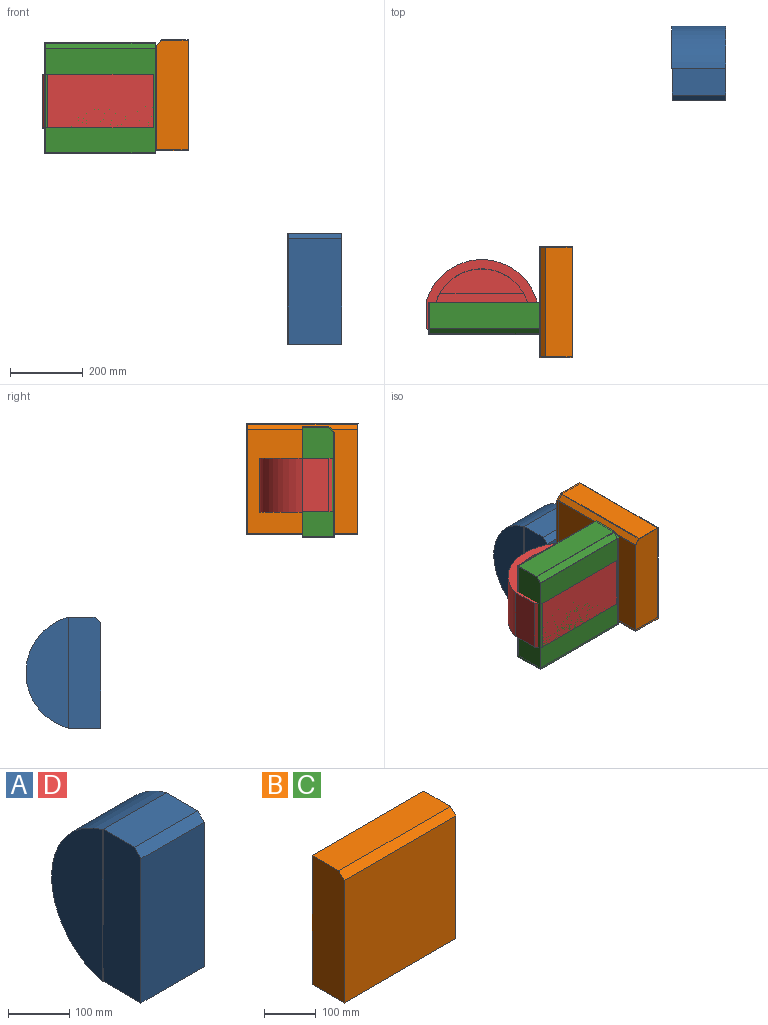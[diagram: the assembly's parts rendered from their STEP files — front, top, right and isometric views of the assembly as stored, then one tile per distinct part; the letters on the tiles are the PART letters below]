
ASSEMBLY  parts=4 mates=2
PART A: 17 faces, bbox 148.6x205x304.8 mm
  f0: plane 304.8x2.03mm, normal (0,-1,0), area 619.4mm2, adj f1,f3,f8
  f1: cylinder r=157.75mm len=304.8mm, axis (-1,0,0), area 61394.1mm2, adj f0,f2,f3,f5,f6
  f2: plane 304.8x205.01mm, normal (1,0,0), area 20286.1mm2, adj f1,f4,f5,f6,f7,f10,f12,f13
  f3: plane 304.8x117.01mm, normal (-1,0,0), area 26381mm2, adj f0,f1
  f4: plane 289.56x146.56mm, normal (0,-1,0), area 42437.3mm2, adj f2,f5,f7,f8
  f5: plane 146.56x88mm, normal (0,0,-1), area 12897mm2, adj f1,f2,f4,f8
  f6: plane 146.56x72.76mm, normal (0,0,1), area 10663.5mm2, adj f1,f2,f7,f8
  f7: plane 146.56x15.24mm, normal (0,-0.71,0.71), area 3158.7mm2, adj f2,f4,f6,f8
  f8: plane 304.8x88mm, normal (-1,0,0), area 26706.1mm2, adj f0,f4,f5,f6,f7
  f9: plane 229.28x2.03mm, normal (0,1,0), area 465.9mm2, adj f10,f11,f16
  f10: cylinder r=132.35mm len=254mm, axis (-1,0,0), area 41789.3mm2, adj f2,f9,f11,f13,f14,f16
  f11: plane 229.28x66.21mm, normal (1,0,0), area 10766.9mm2, adj f9,f10
  f12: plane 253.64x121.16mm, normal (0,1,0), area 30730.4mm2, adj f2,f13,f15,f16
  f13: plane 121.16x59.11mm, normal (0,0,1), area 7162.1mm2, adj f2,f10,f12,f16
  f14: plane 121.16x58.75mm, normal (0,0,-1), area 7118.4mm2, adj f2,f10,f15,f16
  f15: plane 121.16x0.36mm, normal (0,0.71,-0.71), area 61.9mm2, adj f2,f12,f14,f16
  f16: plane 254x88mm, normal (1,0,0), area 22034mm2, adj f9,f10,f12,f13,f14,f15
PART B: 13 faces, bbox 304.8x88x304.8 mm
  f0: plane 304.8x304.8mm, normal (0,1,0), area 3071mm2, adj f1,f3,f4,f5,f7,f9,f10,f11
  f1: plane 304.8x88mm, normal (-1,0,0), area 26706.1mm2, adj f0,f2,f4,f5,f6
  f2: plane 304.8x289.56mm, normal (0,-1,0), area 88257.9mm2, adj f1,f3,f5,f6
  f3: plane 304.8x88mm, normal (1,0,0), area 26706.1mm2, adj f0,f2,f4,f5,f6
  f4: plane 304.8x72.76mm, normal (0,0,1), area 22177mm2, adj f0,f1,f3,f6
  f5: plane 304.8x88mm, normal (0,0,-1), area 26822.2mm2, adj f0,f1,f2,f3
  f6: plane 304.8x15.24mm, normal (0,-0.71,0.71), area 6569.2mm2, adj f1,f2,f3,f4
  f7: plane 299.72x85.46mm, normal (1,0,0), area 25519.3mm2, adj f0,f8,f10,f11,f12
  f8: plane 299.72x285.97mm, normal (0,1,0), area 85710.3mm2, adj f7,f9,f11,f12
  f9: plane 299.72x85.46mm, normal (-1,0,0), area 25519.3mm2, adj f0,f8,f10,f11,f12
  f10: plane 299.72x71.71mm, normal (0,0,-1), area 21492.1mm2, adj f0,f7,f9,f12
  f11: plane 299.72x85.46mm, normal (0,0,1), area 25613.9mm2, adj f0,f7,f8,f9
  f12: plane 299.72x13.75mm, normal (0,0.71,-0.71), area 5829.1mm2, adj f7,f8,f9,f10
PART C: same geometry as B
PART D: same geometry as A
PLACE A t=(-105.52,48.84,70.86)mm
PLACE B rot(axis=(0,0,-1),90deg) t=(-308.2,-578.02,601.44)mm
PLACE C rot(axis=(0.84,0.23,0.49),0deg) t=(-467.15,-593.34,593.82)mm
PLACE D rot(axis=(0,-1,0),90deg) t=(-355.44,-593.34,543.96)mm
MATE fastened B.f2 <-> C.f3  axis (-1,0,0) through (-347.82,-544.96,746.22)mm
MATE revolute D.f4 <-> C.f2  axis (0,-1,0) through (-500.22,-632.96,738.6)mm
